# Revit family: Sink-Semipedestal-Lavatory-KOHLER-Panache-17154W
name_source: partatom
category: Specialty Equipment
revit_build: Autodesk Revit 2017 (Build: 20160225_1515(x64)
units: mm (PartAtom-declared; Revit-internal decimal feet)

## family parameters
Cut with Voids When Loaded = No
Host = Face
OmniClass Number = 23.31.13.00
OmniClass Title = Sinks
Part Type = Normal
Room Calculation Point = No
Round Connector Dimension = Use Diameter
Shared = No

## types (1)
- 0-White
    ADA Compliant = No
    Assembly Code = D2010400
    Date Modified = 04/29/2021
    Default Elevation = 25"
    Description = Semi-pedestal for Candide
    Finish = Kohler-Vitreous_China-0-White
    Height = 11 1/8"
    Length = 12 1/8"
    Manufacturer = KOHLER Co.
    Master Format 2014 = 22 41 16
    Master Format 2014 Name = Residential Lavatories and Sinks
    Material = Vitreous China
    Model = 17154W-0
    Product Name = Panache
    Product Page URL = https://www.kohler.co.uk
    Type = 1
    URL = https://www.kohler.co.uk
    WaterSense Certified = No
    Width = 10 3/4"

## geometry (parser evidence)
native form markers: Sweep x5
no freeform markers — native parametric forms only
